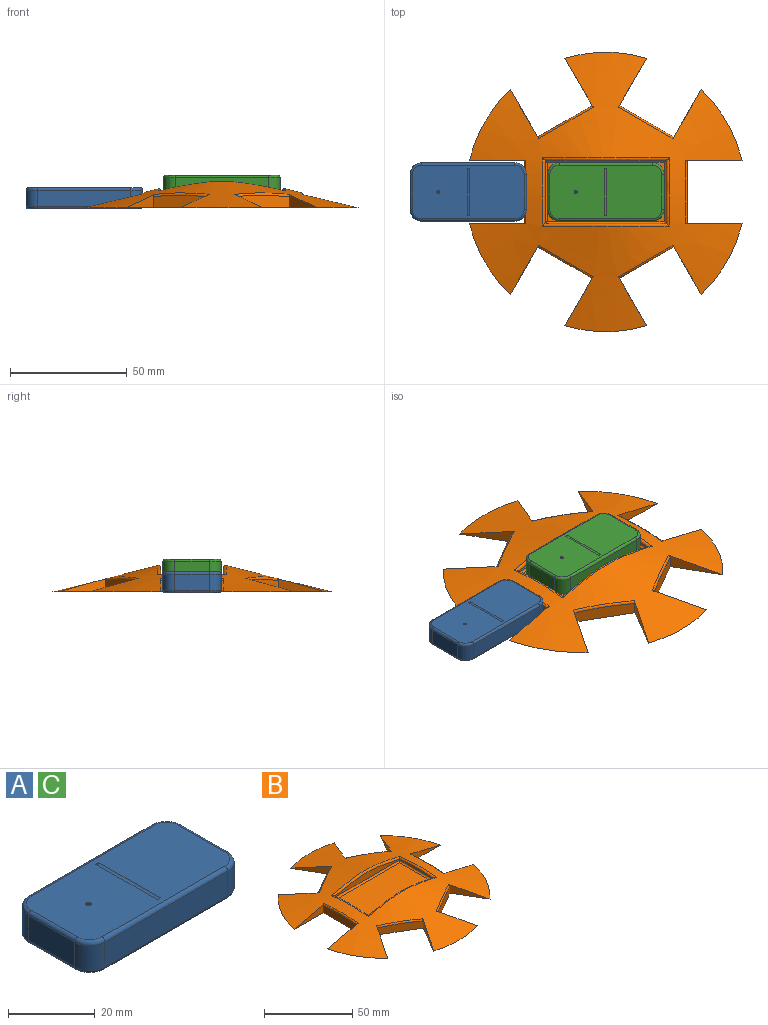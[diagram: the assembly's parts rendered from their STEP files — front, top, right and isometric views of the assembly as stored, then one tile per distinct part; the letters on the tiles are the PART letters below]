
ASSEMBLY  parts=3 mates=1
PART A: 31 faces, bbox 50.8x25.8x9 mm
  f0: plane 48x23mm, normal (0,0,1), area 1069mm2, adj f18,f19,f20,f21,f22,f23,f24,f25
  f1: plane 15x7mm, normal (1,0,0), area 105mm2, adj f6,f9,f16,f23
  f2: plane 40x7mm, normal (0,1,0), area 280mm2, adj f6,f7,f15,f24
  f3: plane 15x7mm, normal (-1,0,0), area 105mm2, adj f7,f8,f11,f20
  f4: plane 40x7mm, normal (0,-1,0), area 280mm2, adj f8,f9,f12,f19
  f5: plane 48x23mm, normal (0,0,-1), area 1090.3mm2, adj f10,f11,f12,f13,f14,f15,f16,f17
  f6: cylinder r=5mm len=7mm, axis (0,0,-1), area 55mm2, adj f1,f2,f17,f25
  f7: cylinder r=5mm len=7mm, axis (0,0,1), area 55mm2, adj f2,f3,f13,f22
  f8: cylinder r=5mm len=7mm, axis (0,0,-1), area 55mm2, adj f3,f4,f10,f18
  f9: cylinder r=5mm len=7mm, axis (0,0,1), area 55mm2, adj f1,f4,f14,f21
  f10: torus R=4mm, axis (0,0,1), area 11.4mm2, adj f5,f8,f11,f12
  f11: cylinder r=1mm len=15mm, axis (0,1,0), area 23.6mm2, adj f3,f5,f10,f13
  f12: cylinder r=1mm len=40mm, axis (-1,0,0), area 62.8mm2, adj f4,f5,f10,f14
  f13: torus R=4mm, axis (0,0,1), area 11.4mm2, adj f5,f7,f11,f15
  f14: torus R=4mm, axis (0,0,1), area 11.4mm2, adj f5,f9,f12,f16
  f15: cylinder r=1mm len=40mm, axis (1,0,0), area 62.8mm2, adj f2,f5,f13,f17
  f16: cylinder r=1mm len=15mm, axis (0,-1,0), area 23.6mm2, adj f1,f5,f14,f17
  f17: torus R=4mm, axis (0,0,1), area 11.4mm2, adj f5,f6,f15,f16
  f18: torus R=4mm, axis (0,0,1), area 11.4mm2, adj f0,f8,f19,f20
  f19: cylinder r=1mm len=40mm, axis (1,0,0), area 62.8mm2, adj f0,f4,f18,f21
  f20: cylinder r=1mm len=15mm, axis (0,-1,0), area 23.6mm2, adj f0,f3,f18,f22
  f21: torus R=4mm, axis (0,0,1), area 11.4mm2, adj f0,f9,f19,f23
  f22: torus R=4mm, axis (0,0,1), area 11.4mm2, adj f0,f7,f20,f24
  f23: cylinder r=1mm len=15mm, axis (0,1,0), area 23.6mm2, adj f0,f1,f21,f25
  f24: cylinder r=1mm len=40mm, axis (-1,0,0), area 62.8mm2, adj f0,f2,f22,f25
  f25: torus R=4mm, axis (0,0,1), area 11.4mm2, adj f0,f6,f23,f24
  f26: cylinder r=0.8mm len=20mm, axis (0,-1,0), area 21.6mm2, adj f0,f27,f28
  f27: plane 1x0.18mm, normal (0,-1,0), area 0.1mm2, adj f0,f26
  f28: plane 1x0.18mm, normal (0,1,0), area 0.1mm2, adj f0,f26
  f29: sphere r=0.87mm, area 0.5mm2, adj f30
  f30: torus R=0.64mm, axis (0,0,1), area 0.8mm2, adj f0,f29
PART B: 39 faces, bbox 121.7x121.7x13.4 mm
  f0: plane 120x116.92mm, normal (0,0,-1), area 7342.4mm2, adj f1,f7,f8,f9,f10,f11,f12,f13
  f1: cone r=60mm half-angle=76deg, axis (0,0,-1), area 5853mm2, adj f0,f8,f9,f11,f12,f14,f15,f17
  f2: plane 27.01x1.22mm, normal (-1,0,0), area 25.6mm2, adj f3,f5,f34,f35
  f3: plane 52.02x4.35mm, normal (0,-1,0), area 150.1mm2, adj f2,f4,f31,f33,f34,f36
  f4: plane 27.01x1.22mm, normal (1,0,0), area 25.6mm2, adj f3,f5,f31,f38
  f5: plane 52.02x4.35mm, normal (0,1,0), area 150.1mm2, adj f2,f4,f31,f32,f34,f37
  f6: plane 50x25mm, normal (0,0,1), area 1250mm2, adj f35,f36,f37,f38
  f7: plane 27.01x5.47mm, normal (-1,0,0), area 141.8mm2, adj f0,f8,f9,f30
  f8: plane 25.99x7.55mm, normal (0,1,0), area 66.5mm2, adj f0,f1,f7,f30
  f9: plane 25.99x7.55mm, normal (0,-1,0), area 66.5mm2, adj f0,f1,f7,f30
  f10: plane 23.39x13.51mm, normal (-0.5,0.87,0), area 141.8mm2, adj f0,f11,f12,f29
  f11: plane 22.74x13.87mm, normal (0.87,0.5,0), area 66.5mm2, adj f0,f1,f10,f29
  f12: plane 22.74x13.87mm, normal (-0.87,-0.5,0), area 66.5mm2, adj f0,f1,f10,f29
  f13: plane 23.39x13.51mm, normal (0.5,0.87,0), area 141.8mm2, adj f0,f14,f15,f28
  f14: plane 22.74x13.87mm, normal (0.87,-0.5,0), area 66.5mm2, adj f0,f1,f13,f28
  f15: plane 22.74x13.87mm, normal (-0.87,0.5,0), area 66.5mm2, adj f0,f1,f13,f28
  f16: plane 27.01x5.47mm, normal (1,0,0), area 141.8mm2, adj f0,f17,f18,f27
  f17: plane 25.99x7.55mm, normal (0,-1,0), area 66.5mm2, adj f0,f1,f16,f27
  f18: plane 25.99x7.55mm, normal (0,1,0), area 66.5mm2, adj f0,f1,f16,f27
  f19: plane 23.39x13.51mm, normal (0.5,-0.87,0), area 141.8mm2, adj f0,f20,f21,f26
  f20: plane 22.74x13.87mm, normal (-0.87,-0.5,0), area 66.5mm2, adj f0,f1,f19,f26
  f21: plane 22.74x13.87mm, normal (0.87,0.5,0), area 66.5mm2, adj f0,f1,f19,f26
  f22: plane 23.39x13.51mm, normal (-0.5,-0.87,0), area 141.8mm2, adj f0,f23,f24,f25
  f23: plane 22.74x13.87mm, normal (-0.87,0.5,0), area 66.5mm2, adj f0,f1,f22,f25
  f24: plane 22.74x13.87mm, normal (0.87,-0.5,0), area 66.5mm2, adj f0,f1,f22,f25
  f25: bspline ~32.54x19.24mm, area 36mm2, adj f1,f22,f23,f24
  f26: bspline ~32.54x19.24mm, area 36mm2, adj f1,f19,f20,f21
  f27: bspline ~37.14x2.18mm, area 36mm2, adj f1,f16,f17,f18
  f28: bspline ~32.54x19.24mm, area 36mm2, adj f1,f13,f14,f15
  f29: bspline ~32.54x19.24mm, area 36mm2, adj f1,f10,f11,f12
  f30: bspline ~37.14x2.17mm, area 36mm2, adj f1,f7,f8,f9
  f31: bspline ~41.9x3.37mm, area 50.3mm2, adj f1,f3,f4,f5,f32,f33
  f32: bspline ~60.98x6.3mm, area 94.6mm2, adj f1,f5,f31,f34
  f33: bspline ~64.49x6.53mm, area 94.6mm2, adj f1,f3,f31,f34
  f34: bspline ~41.9x3.36mm, area 50.3mm2, adj f1,f2,f3,f5,f32,f33
  f35: cylinder r=1mm len=27mm, axis (0,1,0), area 40.8mm2, adj f2,f6,f36,f37
  f36: cylinder r=1mm len=52mm, axis (-1,0,0), area 80.1mm2, adj f3,f6,f35,f38
  f37: cylinder r=1mm len=52mm, axis (1,0,0), area 80.1mm2, adj f5,f6,f35,f38
  f38: cylinder r=1mm len=27mm, axis (0,-1,0), area 40.8mm2, adj f4,f6,f36,f37
PART C: same geometry as A
PLACE A t=(-108.57,11.41,59.08)mm
PLACE B t=(-49.57,11.41,50.46)mm
PLACE C t=(-49.57,11.41,64.46)mm
MATE fastened B.f1 <-> C.f5  axis (0,0,1) through (-49.57,11.41,55.46)mm
